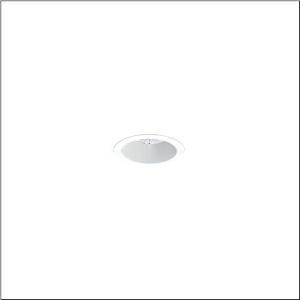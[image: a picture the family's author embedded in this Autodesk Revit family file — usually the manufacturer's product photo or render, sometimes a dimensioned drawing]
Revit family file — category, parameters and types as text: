
# Revit family: lunis_21_s_51db18ea91c
name_source: partatom
category: Lighting Fixtures
units: mm (PartAtom-declared; Revit-internal decimal feet)

## family parameters
Cut with Voids When Loaded = No
Host = Face
Light Source = No
Part Type = Normal
Room Calculation Point = No
Round Connector Dimension = Use Diameter
Shared = No

## types (1)
- --- (1 x LED, 1060 lm, 8 W, 6500K)
    Apparent Load = 8 VA
    CIE Flux Codes = 86 95 99 100 100
    Color Rendering = 80
    Color Temperature = 6500K
    Default Elevation = 1800 mm
    Description = Lunis 21 S, downlight, light control with lens, of PMMA, anti glare with reflector, of PC, light emission: direct distribution, LED rated luminous flux: 950lm, light colour: 830/840/865, with terminal, 5-pole, mains connection: 220..240V, AC, 50..60Hz, housing, round, of diecast aluminium, traffic white (RAL 9016), diameter: 84mm, clamping range: 1..40mm, protection rating (complete): IP20, protection rating (on room side): IP54, insulation class (complete): insulation class II (safety insulation), certification: CE, impact resistance: IK03, packaging unit: 1 piece
    Height = 0 mm  [stored 0 ft]
    Lamp = 1 x LED
    Lamp Light Flux = 1060 lm
    Lamp Power = 8 W
    Lamp count = 1
    Length = 84 mm
    Luminous efficacy = 133 lm/W
    Manufacturer = Siteco
    ModVariant = No
    Model = 51DB18EA91C
    Mounting Place = Ceiling
    Mounting Type = Recessed
    Number of Poles = 1
    OnlyDefault = Yes
    Power Factor = 1
    Product Name = Lunis 21 S
    Product group = downlight
    ProductGroupID = 401
    Protection Class = Protection class II
    Protection Degree = IP 20
    RLX_Detail_Level = 1
    RLX_Emergency_Light_Flux = 0 lm
    RLX_Emergency_Type = 0
    RLX_Emergency_Type_DB = No
    RlxData = <blob elided: 8937 chars, md5=d2bb3dfc>
    Socket = socket
    Standby Power = 0 W
    System Light Flux = 1060 lm
    System Power = 8 W
    Type Comments = individual setting: colour temperature 6500K, luminous flux: 100 % | (OFF | OFF | ON | OFF) | 200 mA
    Type Image = l_1290842.jpg
    URL = http://relux.com
    VarID = @adj_035555
    Voltage = 0 V
    Weight = 0.00 kg
    Width = 0 mm  [stored 0 ft]

note: [stored X ft] marks values corroborated as IEEE doubles in the binary element streams (Revit-internal decimal feet)

## geometry (parser evidence)
native form markers: Sweep x10
no freeform markers — native parametric forms only
